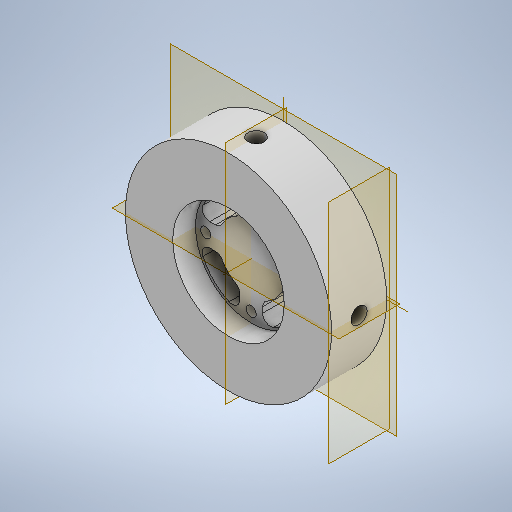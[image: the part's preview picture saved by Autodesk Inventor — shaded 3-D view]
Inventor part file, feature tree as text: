
AUTODESK INVENTOR PART (.ipt)
format: ipt  version: 2025.2 (Build 292293000, 293)  size: 349,184 bytes
history: native  units: in
note: dims shown in document units (in); Inventor stores cm internally (conversion verified against a paired STEP export)
features: sketch x7, extrude x5, plane x1, pattern_circular x1
ambient origin geometry x8: Origin, YZ Plane, XZ Plane, XY Plane, X Axis, Y Axis, Z Axis, Center Point
bodies: Solid1 (feature_tree)
feature tree (14):
  extrude  "Extrusion1"  Depth=0.8563in TaperAngle=0.0deg
  extrude  "Extrusion2"  Depth=0.3543in TaperAngle=0.0deg
  extrude  "Extrusion3"  Depth=0.7087in
  extrude  "Extrusion4"  Depth=0.502in TaperAngle=0.0deg
  plane  "Work Plane1"
  extrude  "Extrusion5"  Depth=0.502in TaperAngle=0.0deg
  pattern_circular  "Circular Pattern1"  [2 undecoded]
  sketch  "Sketch1"  dims[d0=3.2047in d1=0.8563in d2=0.0in]
  sketch  "Sketch2"  dims[d6=0.1575in d7=0.7087in]
  sketch  "Sketch3"  dims[d14=1.5748in d16=360.0deg d18=0.502in d19=0.0in]
  sketch  "Sketch Circular Pattern1"  dims[d3=1.7323in d4=0.3543in d5=0.0in]
  sketch  "Sketch4"  dims[d23=1.6024in]
  sketch  "Sketch Circular Pattern2"  dims[d8=1.5748in d10=360.0deg d12=0.502in d13=0.0in]
  sketch  "Sketch6"  dims[d24=0.25in d27=0.5in d28=0.0in d29=1.5748in d30=360.0deg]
note: 2 required parameter values undecoded (feature->parameter linkage not recoverable at this tier; creation-order binding heuristic only, values carry confidence <= 0.55)
